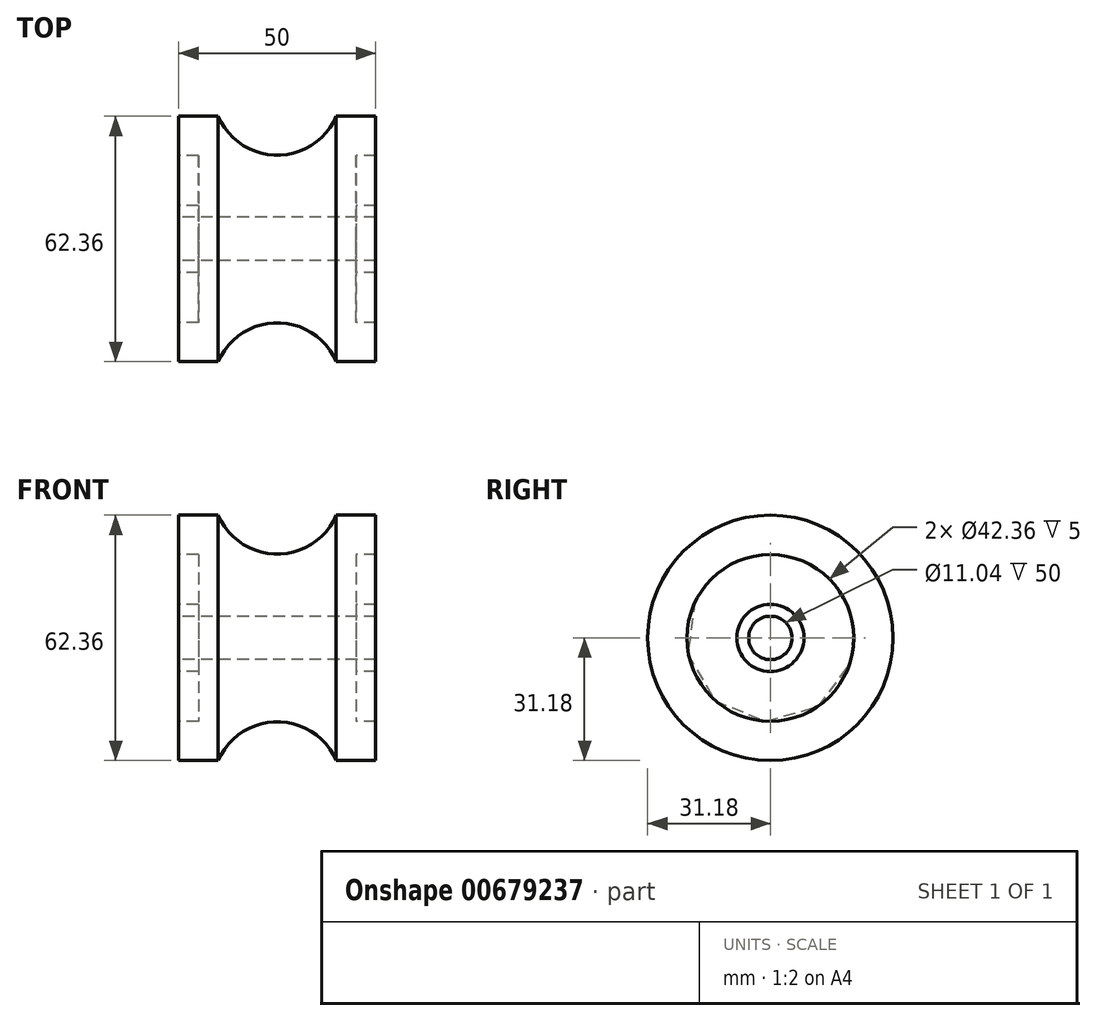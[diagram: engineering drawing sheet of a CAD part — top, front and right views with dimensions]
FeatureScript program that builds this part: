
annotation { "Feature Type Name" : "Feature", "Feature Type Description" : "" }
export const myFeature = defineFeature(function(context is Context, id is Id, definition is map)
    precondition{}
    {
        {
            var Q0;
            Q0=qCreatedBy(makeId("Front.planeOp"),FACE);
            var sketch = newSketch(context, id + "F0", { "sketchPlane" : qUnion([Q0])});
            skLineSegment(sketch, "E0", {"start": v(-48.27, 0) * mm, "end": v(46.51, 0) * mm, "construction": true});
            skLineSegment(sketch, "E1", {"start": v(24.6, 31.18) * mm, "end": v(24.6, 21.18) * mm});
            skLineSegment(sketch, "E2", {"start": v(24.6, 21.18) * mm, "end": v(19.6, 21.18) * mm});
            skLineSegment(sketch, "E3", {"start": v(19.6, 21.18) * mm, "end": v(19.6, 8.52) * mm});
            skLineSegment(sketch, "E4", {"start": v(-25.4, 5.52) * mm, "end": v(-25.4, 8.52) * mm});
            skLineSegment(sketch, "E5", {"start": v(-25.4, 8.52) * mm, "end": v(-20.4, 8.52) * mm});
            skLineSegment(sketch, "E6", {"start": v(-20.4, 8.52) * mm, "end": v(-20.4, 21.18) * mm});
            skLineSegment(sketch, "E7", {"start": v(-20.4, 21.18) * mm, "end": v(-25.4, 21.18) * mm});
            skLineSegment(sketch, "E8", {"start": v(-25.4, 21.18) * mm, "end": v(-25.4, 31.18) * mm});
            skLineSegment(sketch, "E9", {"start": v(19.6, 8.52) * mm, "end": v(24.6, 8.52) * mm});
            skLineSegment(sketch, "E10", {"start": v(24.6, 8.52) * mm, "end": v(24.6, 5.52) * mm});
            skLineSegment(sketch, "E11", {"start": v(24.6, 5.52) * mm, "end": v(-25.4, 5.52) * mm});
            skArc(sketch, "E12", {"start": v(-15.4, 31.18) * mm, "mid": v(-0.4, 21.29) * mm, "end": v(14.6, 31.18) * mm});
            skLineSegment(sketch, "E13", {"start": v(-25.4, 31.18) * mm, "end": v(-15.4, 31.18) * mm});
            skLineSegment(sketch, "E14", {"start": v(14.6, 31.18) * mm, "end": v(24.6, 31.18) * mm});
            skSolve(sketch);
        }
        {
            var Q0;
            Q0 = qSketchRegion(id + "F0", true);
            var Q1;
            Q1=sQuery(id+"F0.wireOp",EDGE,"E0");
            revolve(context, id + "F1", {"entities" : qUnion([Q0]), "axis" : qUnion([Q1]), "revolveType" : RevolveType.FULL});
        }
    });
